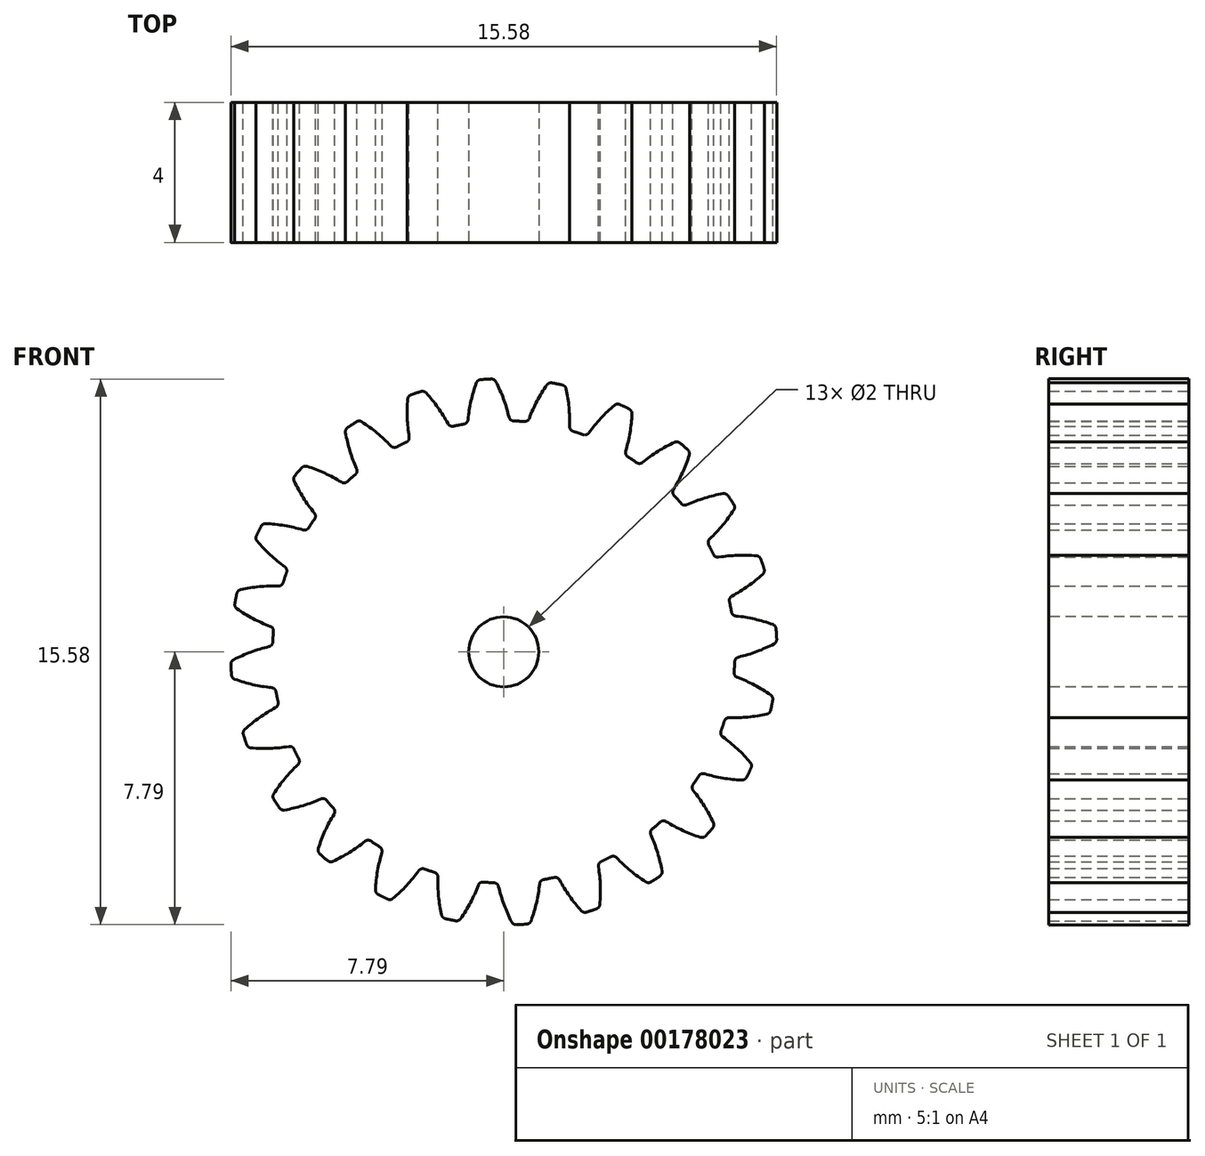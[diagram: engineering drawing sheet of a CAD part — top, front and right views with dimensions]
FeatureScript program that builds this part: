
annotation { "Feature Type Name" : "Feature", "Feature Type Description" : "" }
export const myFeature = defineFeature(function(context is Context, id is Id, definition is map)
    precondition{}
    {
        {
            var Q0;
            Q0=qCreatedBy(makeId("Front.planeOp"),FACE);
            var sketch = newSketch(context, id + "F0", { "sketchPlane" : qUnion([Q0])});
            skCircle(sketch, "E0", {"center": v(0, 0) * mm, "radius": 6.6 * mm, "construction": true});
            skCircle(sketch, "E1", {"center": v(0, 0) * mm, "radius": 7.2 * mm, "construction": true});
            skCircle(sketch, "E2", {"center": v(0, 0) * mm, "radius": 7.8 * mm, "construction": true});
            skLineSegment(sketch, "E3", {"start": v(0, 0) * mm, "end": v(0, 6.31) * mm, "construction": true});
            skCircle(sketch, "E4", {"center": v(0, 7.2) * mm, "radius": 4.32 * mm, "construction": true});
            skCircle(sketch, "E5.cCircle", {"center": v(0, 0) * mm, "radius": 6.31 * mm, "construction": true});
            skLineSegment(sketch, "E5.0", {"start": v(0, 6.31) * mm, "end": v(0.82, 6.26) * mm, "construction": true});
            skLineSegment(sketch, "E5.1", {"start": v(0.82, 6.26) * mm, "end": v(1.63, 6.1) * mm, "construction": true});
            skLineSegment(sketch, "E5.2", {"start": v(1.63, 6.1) * mm, "end": v(2.41, 5.83) * mm, "construction": true});
            skLineSegment(sketch, "E5.3", {"start": v(2.41, 5.83) * mm, "end": v(3.16, 5.46) * mm, "construction": true});
            skLineSegment(sketch, "E5.4", {"start": v(3.16, 5.46) * mm, "end": v(3.84, 5) * mm, "construction": true});
            skLineSegment(sketch, "E5.5", {"start": v(3.84, 5) * mm, "end": v(4.46, 4.46) * mm, "construction": true});
            skLineSegment(sketch, "E5.6", {"start": v(4.46, 4.46) * mm, "end": v(5, 3.84) * mm, "construction": true});
            skLineSegment(sketch, "E5.7", {"start": v(5, 3.84) * mm, "end": v(5.46, 3.16) * mm, "construction": true});
            skLineSegment(sketch, "E5.8", {"start": v(5.46, 3.16) * mm, "end": v(5.83, 2.41) * mm, "construction": true});
            skLineSegment(sketch, "E5.9", {"start": v(5.83, 2.41) * mm, "end": v(6.1, 1.63) * mm, "construction": true});
            skLineSegment(sketch, "E5.10", {"start": v(6.1, 1.63) * mm, "end": v(6.26, 0.82) * mm, "construction": true});
            skLineSegment(sketch, "E5.11", {"start": v(6.26, 0.82) * mm, "end": v(6.31, 0) * mm, "construction": true});
            skLineSegment(sketch, "E5.12", {"start": v(6.31, 0) * mm, "end": v(6.26, -0.82) * mm, "construction": true});
            skLineSegment(sketch, "E5.13", {"start": v(6.26, -0.82) * mm, "end": v(6.1, -1.63) * mm, "construction": true});
            skLineSegment(sketch, "E5.14", {"start": v(6.1, -1.63) * mm, "end": v(5.83, -2.41) * mm, "construction": true});
            skLineSegment(sketch, "E5.15", {"start": v(5.83, -2.41) * mm, "end": v(5.46, -3.16) * mm, "construction": true});
            skLineSegment(sketch, "E5.16", {"start": v(5.46, -3.16) * mm, "end": v(5, -3.84) * mm, "construction": true});
            skLineSegment(sketch, "E5.17", {"start": v(5, -3.84) * mm, "end": v(4.46, -4.46) * mm, "construction": true});
            skLineSegment(sketch, "E5.18", {"start": v(4.46, -4.46) * mm, "end": v(3.84, -5) * mm, "construction": true});
            skLineSegment(sketch, "E5.19", {"start": v(3.84, -5) * mm, "end": v(3.16, -5.46) * mm, "construction": true});
            skLineSegment(sketch, "E5.20", {"start": v(3.16, -5.46) * mm, "end": v(2.41, -5.83) * mm, "construction": true});
            skLineSegment(sketch, "E5.21", {"start": v(2.41, -5.83) * mm, "end": v(1.63, -6.1) * mm, "construction": true});
            skLineSegment(sketch, "E5.22", {"start": v(1.63, -6.1) * mm, "end": v(0.82, -6.26) * mm, "construction": true});
            skLineSegment(sketch, "E5.23", {"start": v(0.82, -6.26) * mm, "end": v(0, -6.31) * mm, "construction": true});
            skLineSegment(sketch, "E5.24", {"start": v(0, -6.31) * mm, "end": v(-0.82, -6.26) * mm, "construction": true});
            skLineSegment(sketch, "E5.25", {"start": v(-0.82, -6.26) * mm, "end": v(-1.63, -6.1) * mm, "construction": true});
            skLineSegment(sketch, "E5.26", {"start": v(-1.63, -6.1) * mm, "end": v(-2.41, -5.83) * mm, "construction": true});
            skLineSegment(sketch, "E5.27", {"start": v(-2.41, -5.83) * mm, "end": v(-3.16, -5.46) * mm, "construction": true});
            skLineSegment(sketch, "E5.28", {"start": v(-3.16, -5.46) * mm, "end": v(-3.84, -5) * mm, "construction": true});
            skLineSegment(sketch, "E5.29", {"start": v(-3.84, -5) * mm, "end": v(-4.46, -4.46) * mm, "construction": true});
            skLineSegment(sketch, "E5.30", {"start": v(-4.46, -4.46) * mm, "end": v(-5, -3.84) * mm, "construction": true});
            skLineSegment(sketch, "E5.31", {"start": v(-5, -3.84) * mm, "end": v(-5.46, -3.16) * mm, "construction": true});
            skLineSegment(sketch, "E5.32", {"start": v(-5.46, -3.16) * mm, "end": v(-5.83, -2.41) * mm, "construction": true});
            skLineSegment(sketch, "E5.33", {"start": v(-5.83, -2.41) * mm, "end": v(-6.1, -1.63) * mm, "construction": true});
            skLineSegment(sketch, "E5.34", {"start": v(-6.1, -1.63) * mm, "end": v(-6.26, -0.82) * mm, "construction": true});
            skLineSegment(sketch, "E5.35", {"start": v(-6.26, -0.82) * mm, "end": v(-6.31, 0) * mm, "construction": true});
            skLineSegment(sketch, "E5.36", {"start": v(-6.31, 0) * mm, "end": v(-6.26, 0.82) * mm, "construction": true});
            skLineSegment(sketch, "E5.37", {"start": v(-6.26, 0.82) * mm, "end": v(-6.1, 1.63) * mm, "construction": true});
            skLineSegment(sketch, "E5.38", {"start": v(-6.1, 1.63) * mm, "end": v(-5.83, 2.41) * mm, "construction": true});
            skLineSegment(sketch, "E5.39", {"start": v(-5.83, 2.41) * mm, "end": v(-5.46, 3.16) * mm, "construction": true});
            skLineSegment(sketch, "E5.40", {"start": v(-5.46, 3.16) * mm, "end": v(-5, 3.84) * mm, "construction": true});
            skLineSegment(sketch, "E5.41", {"start": v(-5, 3.84) * mm, "end": v(-4.46, 4.46) * mm, "construction": true});
            skLineSegment(sketch, "E5.42", {"start": v(-4.46, 4.46) * mm, "end": v(-3.84, 5) * mm, "construction": true});
            skLineSegment(sketch, "E5.43", {"start": v(-3.84, 5) * mm, "end": v(-3.16, 5.46) * mm, "construction": true});
            skLineSegment(sketch, "E5.44", {"start": v(-3.16, 5.46) * mm, "end": v(-2.41, 5.83) * mm, "construction": true});
            skLineSegment(sketch, "E5.45", {"start": v(-2.41, 5.83) * mm, "end": v(-1.63, 6.1) * mm, "construction": true});
            skLineSegment(sketch, "E5.46", {"start": v(-1.63, 6.1) * mm, "end": v(-0.82, 6.26) * mm, "construction": true});
            skLineSegment(sketch, "E5.47", {"start": v(-0.82, 6.26) * mm, "end": v(0, 6.31) * mm, "construction": true});
            skLineSegment(sketch, "E6.0", {"start": v(-0.41, 6.31) * mm, "end": v(0.41, 6.31) * mm});
            skLineSegment(sketch, "E6.1", {"start": v(0.41, 6.31) * mm, "end": v(1.23, 6.2) * mm});
            skLineSegment(sketch, "E6.2", {"start": v(1.23, 6.2) * mm, "end": v(2.03, 5.99) * mm});
            skLineSegment(sketch, "E6.3", {"start": v(2.03, 5.99) * mm, "end": v(2.8, 5.67) * mm});
            skLineSegment(sketch, "E6.4", {"start": v(2.8, 5.67) * mm, "end": v(3.51, 5.26) * mm});
            skLineSegment(sketch, "E6.5", {"start": v(3.51, 5.26) * mm, "end": v(4.17, 4.75) * mm});
            skLineSegment(sketch, "E6.6", {"start": v(4.17, 4.75) * mm, "end": v(4.75, 4.17) * mm});
            skLineSegment(sketch, "E6.7", {"start": v(4.75, 4.17) * mm, "end": v(5.26, 3.51) * mm, "construction": true});
            skLineSegment(sketch, "E6.8", {"start": v(5.26, 3.51) * mm, "end": v(5.67, 2.8) * mm});
            skLineSegment(sketch, "E6.9", {"start": v(5.67, 2.8) * mm, "end": v(5.99, 2.03) * mm});
            skLineSegment(sketch, "E6.10", {"start": v(5.99, 2.03) * mm, "end": v(6.2, 1.23) * mm});
            skLineSegment(sketch, "E6.11", {"start": v(6.2, 1.23) * mm, "end": v(6.31, 0.41) * mm});
            skLineSegment(sketch, "E6.12", {"start": v(6.31, 0.41) * mm, "end": v(6.31, -0.41) * mm});
            skLineSegment(sketch, "E6.13", {"start": v(6.31, -0.41) * mm, "end": v(6.2, -1.23) * mm});
            skLineSegment(sketch, "E6.14", {"start": v(6.2, -1.23) * mm, "end": v(5.99, -2.03) * mm});
            skLineSegment(sketch, "E6.15", {"start": v(5.99, -2.03) * mm, "end": v(5.67, -2.8) * mm});
            skLineSegment(sketch, "E6.16", {"start": v(5.67, -2.8) * mm, "end": v(5.26, -3.51) * mm});
            skLineSegment(sketch, "E6.17", {"start": v(5.26, -3.51) * mm, "end": v(4.75, -4.17) * mm});
            skLineSegment(sketch, "E6.18", {"start": v(4.75, -4.17) * mm, "end": v(4.17, -4.75) * mm});
            skLineSegment(sketch, "E6.19", {"start": v(4.17, -4.75) * mm, "end": v(3.51, -5.26) * mm});
            skLineSegment(sketch, "E6.20", {"start": v(3.51, -5.26) * mm, "end": v(2.8, -5.67) * mm});
            skLineSegment(sketch, "E6.21", {"start": v(2.8, -5.67) * mm, "end": v(2.03, -5.99) * mm});
            skLineSegment(sketch, "E6.22", {"start": v(2.03, -5.99) * mm, "end": v(1.23, -6.2) * mm});
            skLineSegment(sketch, "E6.23", {"start": v(1.23, -6.2) * mm, "end": v(0.41, -6.31) * mm});
            skLineSegment(sketch, "E6.24", {"start": v(0.41, -6.31) * mm, "end": v(-0.41, -6.31) * mm});
            skLineSegment(sketch, "E6.25", {"start": v(-0.41, -6.31) * mm, "end": v(-1.23, -6.2) * mm});
            skLineSegment(sketch, "E6.26", {"start": v(-1.23, -6.2) * mm, "end": v(-2.03, -5.99) * mm});
            skLineSegment(sketch, "E6.27", {"start": v(-2.03, -5.99) * mm, "end": v(-2.8, -5.67) * mm});
            skLineSegment(sketch, "E6.28", {"start": v(-2.8, -5.67) * mm, "end": v(-3.51, -5.26) * mm});
            skLineSegment(sketch, "E6.29", {"start": v(-3.51, -5.26) * mm, "end": v(-4.17, -4.75) * mm});
            skLineSegment(sketch, "E6.30", {"start": v(-4.17, -4.75) * mm, "end": v(-4.75, -4.17) * mm});
            skLineSegment(sketch, "E6.31", {"start": v(-4.75, -4.17) * mm, "end": v(-5.26, -3.51) * mm});
            skLineSegment(sketch, "E6.32", {"start": v(-5.26, -3.51) * mm, "end": v(-5.67, -2.8) * mm});
            skLineSegment(sketch, "E6.33", {"start": v(-5.67, -2.8) * mm, "end": v(-5.99, -2.03) * mm});
            skLineSegment(sketch, "E6.34", {"start": v(-5.99, -2.03) * mm, "end": v(-6.2, -1.23) * mm});
            skLineSegment(sketch, "E6.35", {"start": v(-6.2, -1.23) * mm, "end": v(-6.31, -0.41) * mm});
            skLineSegment(sketch, "E6.36", {"start": v(-6.31, -0.41) * mm, "end": v(-6.31, 0.41) * mm});
            skLineSegment(sketch, "E6.37", {"start": v(-6.31, 0.41) * mm, "end": v(-6.2, 1.23) * mm});
            skLineSegment(sketch, "E6.38", {"start": v(-6.2, 1.23) * mm, "end": v(-5.99, 2.03) * mm});
            skLineSegment(sketch, "E6.39", {"start": v(-5.99, 2.03) * mm, "end": v(-5.67, 2.8) * mm});
            skLineSegment(sketch, "E6.40", {"start": v(-5.67, 2.8) * mm, "end": v(-5.26, 3.51) * mm});
            skLineSegment(sketch, "E6.41", {"start": v(-5.26, 3.51) * mm, "end": v(-4.75, 4.17) * mm});
            skLineSegment(sketch, "E6.42", {"start": v(-4.75, 4.17) * mm, "end": v(-4.17, 4.75) * mm});
            skLineSegment(sketch, "E6.43", {"start": v(-4.17, 4.75) * mm, "end": v(-3.51, 5.26) * mm});
            skLineSegment(sketch, "E6.44", {"start": v(-3.51, 5.26) * mm, "end": v(-2.8, 5.67) * mm});
            skLineSegment(sketch, "E6.45", {"start": v(-2.8, 5.67) * mm, "end": v(-2.03, 5.99) * mm});
            skLineSegment(sketch, "E6.46", {"start": v(-2.03, 5.99) * mm, "end": v(-1.23, 6.2) * mm});
            skLineSegment(sketch, "E6.47", {"start": v(-1.23, 6.2) * mm, "end": v(-0.41, 6.31) * mm});
            skPoint(sketch, "E6.0.midPoint", {"position": v(0, 6.31) * mm});
            skLineSegment(sketch, "E7", {"start": v(0, 7.2) * mm, "end": v(-9.03, 7.2) * mm, "construction": true});
            skLineSegment(sketch, "E8", {"start": v(0, 7.2) * mm, "end": v(-8.97, 3.93) * mm, "construction": true});
            skCircle(sketch, "E9", {"center": v(-4.06, 5.72) * mm, "radius": 4.32 * mm, "construction": true});
            skArc(sketch, "E10", {"start": v(-0.23, 7.71) * mm, "mid": v(0, 7.22) * mm, "end": v(0.15, 6.7) * mm});
            skLineSegment(sketch, "E11", {"start": v(0, 0) * mm, "end": v(-0.41, 6.31) * mm, "construction": true});
            skArc(sketch, "E12.MirrorCS", {"start": v(-0.78, 7.68) * mm, "mid": v(-0.93, 7.16) * mm, "end": v(-1.02, 6.63) * mm});
            skArc(sketch, "E13", {"start": v(-0.66, 7.77) * mm, "mid": v(-0.51, 7.78) * mm, "end": v(-0.36, 7.8) * mm});
            skArc(sketch, "E14", {"start": v(-1.14, 6.5) * mm, "mid": v(0.43, -6.59) * mm, "end": v(0.28, 6.6) * mm});
            skPoint(sketch, "E15.visualSharp", {"position": v(-1.03, 6.52) * mm});
            skArc(sketch, "E15.filletArc", {"start": v(-1.14, 6.5) * mm, "mid": v(-1.06, 6.54) * mm, "end": v(-1.02, 6.63) * mm});
            skPoint(sketch, "E16.visualSharp", {"position": v(0.17, 6.6) * mm});
            skArc(sketch, "E16.filletArc", {"start": v(0.15, 6.7) * mm, "mid": v(0.2, 6.63) * mm, "end": v(0.28, 6.6) * mm});
            skPoint(sketch, "E17.visualSharp", {"position": v(-0.75, 7.76) * mm});
            skArc(sketch, "E17.filletArc", {"start": v(-0.66, 7.77) * mm, "mid": v(-0.74, 7.74) * mm, "end": v(-0.78, 7.68) * mm});
            skPoint(sketch, "E18.visualSharp", {"position": v(-0.27, 7.8) * mm});
            skArc(sketch, "E18.filletArc", {"start": v(-0.23, 7.71) * mm, "mid": v(-0.28, 7.77) * mm, "end": v(-0.36, 7.8) * mm});
            skArc(sketch, "E19.1.0", {"start": v(-2.78, 5.98) * mm, "mid": v(-2.72, 6.05) * mm, "end": v(-2.7, 6.14) * mm});
            skArc(sketch, "E19.1.1", {"start": v(-2.74, 7.21) * mm, "mid": v(-2.76, 6.67) * mm, "end": v(-2.7, 6.14) * mm});
            skArc(sketch, "E19.1.2", {"start": v(-2.65, 7.34) * mm, "mid": v(-2.71, 7.29) * mm, "end": v(-2.74, 7.21) * mm});
            skArc(sketch, "E19.1.3", {"start": v(-2.65, 7.34) * mm, "mid": v(-2.5, 7.39) * mm, "end": v(-2.36, 7.43) * mm});
            skArc(sketch, "E19.1.4", {"start": v(-2.21, 7.4) * mm, "mid": v(-2.28, 7.43) * mm, "end": v(-2.36, 7.43) * mm});
            skArc(sketch, "E19.1.5", {"start": v(-2.21, 7.4) * mm, "mid": v(-1.88, 6.97) * mm, "end": v(-1.6, 6.51) * mm});
            skArc(sketch, "E19.1.6", {"start": v(-1.6, 6.51) * mm, "mid": v(-1.53, 6.45) * mm, "end": v(-1.43, 6.44) * mm});
            skArc(sketch, "E19.2.0", {"start": v(-4.24, 5.06) * mm, "mid": v(-4.19, 5.14) * mm, "end": v(-4.2, 5.23) * mm});
            skArc(sketch, "E19.2.1", {"start": v(-4.52, 6.26) * mm, "mid": v(-4.39, 5.73) * mm, "end": v(-4.2, 5.23) * mm});
            skArc(sketch, "E19.2.2", {"start": v(-4.46, 6.4) * mm, "mid": v(-4.5, 6.34) * mm, "end": v(-4.52, 6.26) * mm});
            skArc(sketch, "E19.2.3", {"start": v(-4.46, 6.4) * mm, "mid": v(-4.33, 6.49) * mm, "end": v(-4.2, 6.57) * mm});
            skArc(sketch, "E19.2.4", {"start": v(-4.05, 6.57) * mm, "mid": v(-4.13, 6.6) * mm, "end": v(-4.2, 6.57) * mm});
            skArc(sketch, "E19.2.5", {"start": v(-4.05, 6.57) * mm, "mid": v(-3.62, 6.25) * mm, "end": v(-3.23, 5.88) * mm});
            skArc(sketch, "E19.2.6", {"start": v(-3.23, 5.88) * mm, "mid": v(-3.14, 5.84) * mm, "end": v(-3.05, 5.85) * mm});
            skArc(sketch, "E19.3.0", {"start": v(-5.4, 3.8) * mm, "mid": v(-5.38, 3.88) * mm, "end": v(-5.4, 3.96) * mm});
            skArc(sketch, "E19.3.1", {"start": v(-5.98, 4.88) * mm, "mid": v(-5.72, 4.4) * mm, "end": v(-5.4, 3.96) * mm});
            skArc(sketch, "E19.3.2", {"start": v(-5.96, 5.03) * mm, "mid": v(-6, 4.96) * mm, "end": v(-5.98, 4.88) * mm});
            skArc(sketch, "E19.3.3", {"start": v(-5.96, 5.03) * mm, "mid": v(-5.86, 5.14) * mm, "end": v(-5.76, 5.25) * mm});
            skArc(sketch, "E19.3.4", {"start": v(-5.61, 5.3) * mm, "mid": v(-5.7, 5.3) * mm, "end": v(-5.76, 5.25) * mm});
            skArc(sketch, "E19.3.5", {"start": v(-5.61, 5.3) * mm, "mid": v(-5.11, 5.1) * mm, "end": v(-4.64, 4.85) * mm});
            skArc(sketch, "E19.3.6", {"start": v(-4.64, 4.85) * mm, "mid": v(-4.55, 4.82) * mm, "end": v(-4.46, 4.86) * mm});
            skArc(sketch, "E19.4.0", {"start": v(-6.2, 2.26) * mm, "mid": v(-6.2, 2.36) * mm, "end": v(-6.25, 2.43) * mm});
            skArc(sketch, "E19.4.1", {"start": v(-7.04, 3.16) * mm, "mid": v(-6.67, 2.77) * mm, "end": v(-6.25, 2.43) * mm});
            skArc(sketch, "E19.4.2", {"start": v(-7.06, 3.31) * mm, "mid": v(-7.07, 3.23) * mm, "end": v(-7.04, 3.16) * mm});
            skArc(sketch, "E19.4.3", {"start": v(-7.06, 3.31) * mm, "mid": v(-7, 3.45) * mm, "end": v(-6.93, 3.58) * mm});
            skArc(sketch, "E19.4.4", {"start": v(-6.8, 3.66) * mm, "mid": v(-6.87, 3.64) * mm, "end": v(-6.93, 3.58) * mm});
            skArc(sketch, "E19.4.5", {"start": v(-6.8, 3.66) * mm, "mid": v(-6.26, 3.6) * mm, "end": v(-5.73, 3.48) * mm});
            skArc(sketch, "E19.4.6", {"start": v(-5.73, 3.48) * mm, "mid": v(-5.64, 3.48) * mm, "end": v(-5.57, 3.54) * mm});
            skArc(sketch, "E19.5.0", {"start": v(-6.57, 0.58) * mm, "mid": v(-6.6, 0.67) * mm, "end": v(-6.67, 0.73) * mm});
            skArc(sketch, "E19.5.1", {"start": v(-7.62, 1.23) * mm, "mid": v(-7.16, 0.95) * mm, "end": v(-6.67, 0.73) * mm});
            skArc(sketch, "E19.5.2", {"start": v(-7.68, 1.37) * mm, "mid": v(-7.67, 1.3) * mm, "end": v(-7.62, 1.23) * mm});
            skArc(sketch, "E19.5.3", {"start": v(-7.68, 1.37) * mm, "mid": v(-7.65, 1.52) * mm, "end": v(-7.62, 1.67) * mm});
            skArc(sketch, "E19.5.4", {"start": v(-7.5, 1.78) * mm, "mid": v(-7.58, 1.74) * mm, "end": v(-7.62, 1.67) * mm});
            skArc(sketch, "E19.5.5", {"start": v(-7.5, 1.78) * mm, "mid": v(-6.98, 1.86) * mm, "end": v(-6.44, 1.88) * mm});
            skArc(sketch, "E19.5.6", {"start": v(-6.44, 1.88) * mm, "mid": v(-6.35, 1.9) * mm, "end": v(-6.3, 1.98) * mm});
            skArc(sketch, "E19.6.0", {"start": v(-6.5, -1.14) * mm, "mid": v(-6.54, -1.06) * mm, "end": v(-6.63, -1.02) * mm});
            skArc(sketch, "E19.6.1", {"start": v(-7.68, -0.78) * mm, "mid": v(-7.16, -0.93) * mm, "end": v(-6.63, -1.02) * mm});
            skArc(sketch, "E19.6.2", {"start": v(-7.77, -0.66) * mm, "mid": v(-7.74, -0.74) * mm, "end": v(-7.68, -0.78) * mm});
            skArc(sketch, "E19.6.3", {"start": v(-7.77, -0.66) * mm, "mid": v(-7.78, -0.51) * mm, "end": v(-7.8, -0.36) * mm});
            skArc(sketch, "E19.6.4", {"start": v(-7.71, -0.23) * mm, "mid": v(-7.77, -0.28) * mm, "end": v(-7.8, -0.36) * mm});
            skArc(sketch, "E19.6.5", {"start": v(-7.71, -0.23) * mm, "mid": v(-7.22, 0) * mm, "end": v(-6.7, 0.15) * mm});
            skArc(sketch, "E19.6.6", {"start": v(-6.7, 0.15) * mm, "mid": v(-6.63, 0.2) * mm, "end": v(-6.6, 0.28) * mm});
            skArc(sketch, "E19.7.0", {"start": v(-5.98, -2.78) * mm, "mid": v(-6.05, -2.72) * mm, "end": v(-6.14, -2.7) * mm});
            skArc(sketch, "E19.7.1", {"start": v(-7.21, -2.74) * mm, "mid": v(-6.67, -2.76) * mm, "end": v(-6.14, -2.7) * mm});
            skArc(sketch, "E19.7.2", {"start": v(-7.34, -2.65) * mm, "mid": v(-7.29, -2.71) * mm, "end": v(-7.21, -2.74) * mm});
            skArc(sketch, "E19.7.3", {"start": v(-7.34, -2.65) * mm, "mid": v(-7.39, -2.5) * mm, "end": v(-7.43, -2.36) * mm});
            skArc(sketch, "E19.7.4", {"start": v(-7.4, -2.21) * mm, "mid": v(-7.43, -2.28) * mm, "end": v(-7.43, -2.36) * mm});
            skArc(sketch, "E19.7.5", {"start": v(-7.4, -2.21) * mm, "mid": v(-6.97, -1.88) * mm, "end": v(-6.51, -1.6) * mm});
            skArc(sketch, "E19.7.6", {"start": v(-6.51, -1.6) * mm, "mid": v(-6.45, -1.53) * mm, "end": v(-6.44, -1.43) * mm});
            skArc(sketch, "E19.8.0", {"start": v(-5.06, -4.24) * mm, "mid": v(-5.14, -4.19) * mm, "end": v(-5.23, -4.2) * mm});
            skArc(sketch, "E19.8.1", {"start": v(-6.26, -4.52) * mm, "mid": v(-5.73, -4.39) * mm, "end": v(-5.23, -4.2) * mm});
            skArc(sketch, "E19.8.2", {"start": v(-6.4, -4.46) * mm, "mid": v(-6.34, -4.5) * mm, "end": v(-6.26, -4.52) * mm});
            skArc(sketch, "E19.8.3", {"start": v(-6.4, -4.46) * mm, "mid": v(-6.49, -4.33) * mm, "end": v(-6.57, -4.2) * mm});
            skArc(sketch, "E19.8.4", {"start": v(-6.57, -4.05) * mm, "mid": v(-6.6, -4.13) * mm, "end": v(-6.57, -4.2) * mm});
            skArc(sketch, "E19.8.5", {"start": v(-6.57, -4.05) * mm, "mid": v(-6.25, -3.62) * mm, "end": v(-5.88, -3.23) * mm});
            skArc(sketch, "E19.8.6", {"start": v(-5.88, -3.23) * mm, "mid": v(-5.84, -3.14) * mm, "end": v(-5.85, -3.05) * mm});
            skArc(sketch, "E19.9.0", {"start": v(-3.8, -5.4) * mm, "mid": v(-3.88, -5.38) * mm, "end": v(-3.96, -5.4) * mm});
            skArc(sketch, "E19.9.1", {"start": v(-4.88, -5.98) * mm, "mid": v(-4.4, -5.72) * mm, "end": v(-3.96, -5.4) * mm});
            skArc(sketch, "E19.9.2", {"start": v(-5.03, -5.96) * mm, "mid": v(-4.96, -6) * mm, "end": v(-4.88, -5.98) * mm});
            skArc(sketch, "E19.9.3", {"start": v(-5.03, -5.96) * mm, "mid": v(-5.14, -5.86) * mm, "end": v(-5.25, -5.76) * mm});
            skArc(sketch, "E19.9.4", {"start": v(-5.3, -5.61) * mm, "mid": v(-5.3, -5.7) * mm, "end": v(-5.25, -5.76) * mm});
            skArc(sketch, "E19.9.5", {"start": v(-5.3, -5.61) * mm, "mid": v(-5.1, -5.11) * mm, "end": v(-4.85, -4.64) * mm});
            skArc(sketch, "E19.9.6", {"start": v(-4.85, -4.64) * mm, "mid": v(-4.82, -4.55) * mm, "end": v(-4.86, -4.46) * mm});
            skArc(sketch, "E19.10.0", {"start": v(-2.26, -6.2) * mm, "mid": v(-2.36, -6.2) * mm, "end": v(-2.43, -6.25) * mm});
            skArc(sketch, "E19.10.1", {"start": v(-3.16, -7.04) * mm, "mid": v(-2.77, -6.67) * mm, "end": v(-2.43, -6.25) * mm});
            skArc(sketch, "E19.10.2", {"start": v(-3.31, -7.06) * mm, "mid": v(-3.23, -7.07) * mm, "end": v(-3.16, -7.04) * mm});
            skArc(sketch, "E19.10.3", {"start": v(-3.31, -7.06) * mm, "mid": v(-3.45, -7) * mm, "end": v(-3.58, -6.93) * mm});
            skArc(sketch, "E19.10.4", {"start": v(-3.66, -6.8) * mm, "mid": v(-3.64, -6.87) * mm, "end": v(-3.58, -6.93) * mm});
            skArc(sketch, "E19.10.5", {"start": v(-3.66, -6.8) * mm, "mid": v(-3.6, -6.26) * mm, "end": v(-3.48, -5.73) * mm});
            skArc(sketch, "E19.10.6", {"start": v(-3.48, -5.73) * mm, "mid": v(-3.48, -5.64) * mm, "end": v(-3.54, -5.57) * mm});
            skArc(sketch, "E19.11.0", {"start": v(-0.58, -6.57) * mm, "mid": v(-0.67, -6.6) * mm, "end": v(-0.73, -6.67) * mm});
            skArc(sketch, "E19.11.1", {"start": v(-1.23, -7.62) * mm, "mid": v(-0.95, -7.16) * mm, "end": v(-0.73, -6.67) * mm});
            skArc(sketch, "E19.11.2", {"start": v(-1.37, -7.68) * mm, "mid": v(-1.3, -7.67) * mm, "end": v(-1.23, -7.62) * mm});
            skArc(sketch, "E19.11.3", {"start": v(-1.37, -7.68) * mm, "mid": v(-1.52, -7.65) * mm, "end": v(-1.67, -7.62) * mm});
            skArc(sketch, "E19.11.4", {"start": v(-1.78, -7.5) * mm, "mid": v(-1.74, -7.58) * mm, "end": v(-1.67, -7.62) * mm});
            skArc(sketch, "E19.11.5", {"start": v(-1.78, -7.5) * mm, "mid": v(-1.86, -6.98) * mm, "end": v(-1.88, -6.44) * mm});
            skArc(sketch, "E19.11.6", {"start": v(-1.88, -6.44) * mm, "mid": v(-1.9, -6.35) * mm, "end": v(-1.98, -6.3) * mm});
            skArc(sketch, "E19.12.0", {"start": v(1.14, -6.5) * mm, "mid": v(1.06, -6.54) * mm, "end": v(1.02, -6.63) * mm});
            skArc(sketch, "E19.12.1", {"start": v(0.78, -7.68) * mm, "mid": v(0.93, -7.16) * mm, "end": v(1.02, -6.63) * mm});
            skArc(sketch, "E19.12.2", {"start": v(0.66, -7.77) * mm, "mid": v(0.74, -7.74) * mm, "end": v(0.78, -7.68) * mm});
            skArc(sketch, "E19.12.3", {"start": v(0.66, -7.77) * mm, "mid": v(0.51, -7.78) * mm, "end": v(0.36, -7.8) * mm});
            skArc(sketch, "E19.12.4", {"start": v(0.23, -7.71) * mm, "mid": v(0.28, -7.77) * mm, "end": v(0.36, -7.8) * mm});
            skArc(sketch, "E19.12.5", {"start": v(0.23, -7.71) * mm, "mid": v(0, -7.22) * mm, "end": v(-0.15, -6.7) * mm});
            skArc(sketch, "E19.12.6", {"start": v(-0.15, -6.7) * mm, "mid": v(-0.2, -6.63) * mm, "end": v(-0.28, -6.6) * mm});
            skArc(sketch, "E19.13.0", {"start": v(2.78, -5.98) * mm, "mid": v(2.72, -6.05) * mm, "end": v(2.7, -6.14) * mm});
            skArc(sketch, "E19.13.1", {"start": v(2.74, -7.21) * mm, "mid": v(2.76, -6.67) * mm, "end": v(2.7, -6.14) * mm});
            skArc(sketch, "E19.13.2", {"start": v(2.65, -7.34) * mm, "mid": v(2.71, -7.29) * mm, "end": v(2.74, -7.21) * mm});
            skArc(sketch, "E19.13.3", {"start": v(2.65, -7.34) * mm, "mid": v(2.5, -7.39) * mm, "end": v(2.36, -7.43) * mm});
            skArc(sketch, "E19.13.4", {"start": v(2.21, -7.4) * mm, "mid": v(2.28, -7.43) * mm, "end": v(2.36, -7.43) * mm});
            skArc(sketch, "E19.13.5", {"start": v(2.21, -7.4) * mm, "mid": v(1.88, -6.97) * mm, "end": v(1.6, -6.51) * mm});
            skArc(sketch, "E19.13.6", {"start": v(1.6, -6.51) * mm, "mid": v(1.53, -6.45) * mm, "end": v(1.43, -6.44) * mm});
            skArc(sketch, "E19.14.0", {"start": v(4.24, -5.06) * mm, "mid": v(4.19, -5.14) * mm, "end": v(4.2, -5.23) * mm});
            skArc(sketch, "E19.14.1", {"start": v(4.52, -6.26) * mm, "mid": v(4.39, -5.73) * mm, "end": v(4.2, -5.23) * mm});
            skArc(sketch, "E19.14.2", {"start": v(4.46, -6.4) * mm, "mid": v(4.5, -6.34) * mm, "end": v(4.52, -6.26) * mm});
            skArc(sketch, "E19.14.3", {"start": v(4.46, -6.4) * mm, "mid": v(4.33, -6.49) * mm, "end": v(4.2, -6.57) * mm});
            skArc(sketch, "E19.14.4", {"start": v(4.05, -6.57) * mm, "mid": v(4.13, -6.6) * mm, "end": v(4.2, -6.57) * mm});
            skArc(sketch, "E19.14.5", {"start": v(4.05, -6.57) * mm, "mid": v(3.62, -6.25) * mm, "end": v(3.23, -5.88) * mm});
            skArc(sketch, "E19.14.6", {"start": v(3.23, -5.88) * mm, "mid": v(3.14, -5.84) * mm, "end": v(3.05, -5.85) * mm});
            skArc(sketch, "E19.15.0", {"start": v(5.4, -3.8) * mm, "mid": v(5.38, -3.88) * mm, "end": v(5.4, -3.96) * mm});
            skArc(sketch, "E19.15.1", {"start": v(5.98, -4.88) * mm, "mid": v(5.72, -4.4) * mm, "end": v(5.4, -3.96) * mm});
            skArc(sketch, "E19.15.2", {"start": v(5.96, -5.03) * mm, "mid": v(6, -4.96) * mm, "end": v(5.98, -4.88) * mm});
            skArc(sketch, "E19.15.3", {"start": v(5.96, -5.03) * mm, "mid": v(5.86, -5.14) * mm, "end": v(5.76, -5.25) * mm});
            skArc(sketch, "E19.15.4", {"start": v(5.61, -5.3) * mm, "mid": v(5.7, -5.3) * mm, "end": v(5.76, -5.25) * mm});
            skArc(sketch, "E19.15.5", {"start": v(5.61, -5.3) * mm, "mid": v(5.11, -5.1) * mm, "end": v(4.64, -4.85) * mm});
            skArc(sketch, "E19.15.6", {"start": v(4.64, -4.85) * mm, "mid": v(4.55, -4.82) * mm, "end": v(4.46, -4.86) * mm});
            skArc(sketch, "E19.16.0", {"start": v(6.2, -2.26) * mm, "mid": v(6.2, -2.36) * mm, "end": v(6.25, -2.43) * mm});
            skArc(sketch, "E19.16.1", {"start": v(7.04, -3.16) * mm, "mid": v(6.67, -2.77) * mm, "end": v(6.25, -2.43) * mm});
            skArc(sketch, "E19.16.2", {"start": v(7.06, -3.31) * mm, "mid": v(7.07, -3.23) * mm, "end": v(7.04, -3.16) * mm});
            skArc(sketch, "E19.16.3", {"start": v(7.06, -3.31) * mm, "mid": v(7, -3.45) * mm, "end": v(6.93, -3.58) * mm});
            skArc(sketch, "E19.16.4", {"start": v(6.8, -3.66) * mm, "mid": v(6.87, -3.64) * mm, "end": v(6.93, -3.58) * mm});
            skArc(sketch, "E19.16.5", {"start": v(6.8, -3.66) * mm, "mid": v(6.26, -3.6) * mm, "end": v(5.73, -3.48) * mm});
            skArc(sketch, "E19.16.6", {"start": v(5.73, -3.48) * mm, "mid": v(5.64, -3.48) * mm, "end": v(5.57, -3.54) * mm});
            skArc(sketch, "E19.17.0", {"start": v(6.57, -0.58) * mm, "mid": v(6.6, -0.67) * mm, "end": v(6.67, -0.73) * mm});
            skArc(sketch, "E19.17.1", {"start": v(7.62, -1.23) * mm, "mid": v(7.16, -0.95) * mm, "end": v(6.67, -0.73) * mm});
            skArc(sketch, "E19.17.2", {"start": v(7.68, -1.37) * mm, "mid": v(7.67, -1.3) * mm, "end": v(7.62, -1.23) * mm});
            skArc(sketch, "E19.17.3", {"start": v(7.68, -1.37) * mm, "mid": v(7.65, -1.52) * mm, "end": v(7.62, -1.67) * mm});
            skArc(sketch, "E19.17.4", {"start": v(7.5, -1.78) * mm, "mid": v(7.58, -1.74) * mm, "end": v(7.62, -1.67) * mm});
            skArc(sketch, "E19.17.5", {"start": v(7.5, -1.78) * mm, "mid": v(6.98, -1.86) * mm, "end": v(6.44, -1.88) * mm});
            skArc(sketch, "E19.17.6", {"start": v(6.44, -1.88) * mm, "mid": v(6.35, -1.9) * mm, "end": v(6.3, -1.98) * mm});
            skArc(sketch, "E19.18.0", {"start": v(6.5, 1.14) * mm, "mid": v(6.54, 1.06) * mm, "end": v(6.63, 1.02) * mm});
            skArc(sketch, "E19.18.1", {"start": v(7.68, 0.78) * mm, "mid": v(7.16, 0.93) * mm, "end": v(6.63, 1.02) * mm});
            skArc(sketch, "E19.18.2", {"start": v(7.77, 0.66) * mm, "mid": v(7.74, 0.74) * mm, "end": v(7.68, 0.78) * mm});
            skArc(sketch, "E19.18.3", {"start": v(7.77, 0.66) * mm, "mid": v(7.78, 0.51) * mm, "end": v(7.8, 0.36) * mm});
            skArc(sketch, "E19.18.4", {"start": v(7.71, 0.23) * mm, "mid": v(7.77, 0.28) * mm, "end": v(7.8, 0.36) * mm});
            skArc(sketch, "E19.18.5", {"start": v(7.71, 0.23) * mm, "mid": v(7.22, 0) * mm, "end": v(6.7, -0.15) * mm});
            skArc(sketch, "E19.18.6", {"start": v(6.7, -0.15) * mm, "mid": v(6.63, -0.2) * mm, "end": v(6.6, -0.28) * mm});
            skArc(sketch, "E19.19.0", {"start": v(5.98, 2.78) * mm, "mid": v(6.05, 2.72) * mm, "end": v(6.14, 2.7) * mm});
            skArc(sketch, "E19.19.1", {"start": v(7.21, 2.74) * mm, "mid": v(6.67, 2.76) * mm, "end": v(6.14, 2.7) * mm});
            skArc(sketch, "E19.19.2", {"start": v(7.34, 2.65) * mm, "mid": v(7.29, 2.71) * mm, "end": v(7.21, 2.74) * mm});
            skArc(sketch, "E19.19.3", {"start": v(7.34, 2.65) * mm, "mid": v(7.39, 2.5) * mm, "end": v(7.43, 2.36) * mm});
            skArc(sketch, "E19.19.4", {"start": v(7.4, 2.21) * mm, "mid": v(7.43, 2.28) * mm, "end": v(7.43, 2.36) * mm});
            skArc(sketch, "E19.19.5", {"start": v(7.4, 2.21) * mm, "mid": v(6.97, 1.88) * mm, "end": v(6.51, 1.6) * mm});
            skArc(sketch, "E19.19.6", {"start": v(6.51, 1.6) * mm, "mid": v(6.45, 1.53) * mm, "end": v(6.44, 1.43) * mm});
            skArc(sketch, "E19.20.0", {"start": v(5.06, 4.24) * mm, "mid": v(5.14, 4.19) * mm, "end": v(5.23, 4.2) * mm});
            skArc(sketch, "E19.20.1", {"start": v(6.26, 4.52) * mm, "mid": v(5.73, 4.39) * mm, "end": v(5.23, 4.2) * mm});
            skArc(sketch, "E19.20.2", {"start": v(6.4, 4.46) * mm, "mid": v(6.34, 4.5) * mm, "end": v(6.26, 4.52) * mm});
            skArc(sketch, "E19.20.3", {"start": v(6.4, 4.46) * mm, "mid": v(6.49, 4.33) * mm, "end": v(6.57, 4.2) * mm});
            skArc(sketch, "E19.20.4", {"start": v(6.57, 4.05) * mm, "mid": v(6.6, 4.13) * mm, "end": v(6.57, 4.2) * mm});
            skArc(sketch, "E19.20.5", {"start": v(6.57, 4.05) * mm, "mid": v(6.25, 3.62) * mm, "end": v(5.88, 3.23) * mm});
            skArc(sketch, "E19.20.6", {"start": v(5.88, 3.23) * mm, "mid": v(5.84, 3.14) * mm, "end": v(5.85, 3.05) * mm});
            skArc(sketch, "E19.21.0", {"start": v(3.8, 5.4) * mm, "mid": v(3.88, 5.38) * mm, "end": v(3.96, 5.4) * mm});
            skArc(sketch, "E19.21.1", {"start": v(4.88, 5.98) * mm, "mid": v(4.4, 5.72) * mm, "end": v(3.96, 5.4) * mm});
            skArc(sketch, "E19.21.2", {"start": v(5.03, 5.96) * mm, "mid": v(4.96, 6) * mm, "end": v(4.88, 5.98) * mm});
            skArc(sketch, "E19.21.3", {"start": v(5.03, 5.96) * mm, "mid": v(5.14, 5.86) * mm, "end": v(5.25, 5.76) * mm});
            skArc(sketch, "E19.21.4", {"start": v(5.3, 5.61) * mm, "mid": v(5.3, 5.7) * mm, "end": v(5.25, 5.76) * mm});
            skArc(sketch, "E19.21.5", {"start": v(5.3, 5.61) * mm, "mid": v(5.1, 5.11) * mm, "end": v(4.85, 4.64) * mm});
            skArc(sketch, "E19.21.6", {"start": v(4.85, 4.64) * mm, "mid": v(4.82, 4.55) * mm, "end": v(4.86, 4.46) * mm});
            skArc(sketch, "E19.22.0", {"start": v(2.26, 6.2) * mm, "mid": v(2.36, 6.2) * mm, "end": v(2.43, 6.25) * mm});
            skArc(sketch, "E19.22.1", {"start": v(3.16, 7.04) * mm, "mid": v(2.77, 6.67) * mm, "end": v(2.43, 6.25) * mm});
            skArc(sketch, "E19.22.2", {"start": v(3.31, 7.06) * mm, "mid": v(3.23, 7.07) * mm, "end": v(3.16, 7.04) * mm});
            skArc(sketch, "E19.22.3", {"start": v(3.31, 7.06) * mm, "mid": v(3.45, 7) * mm, "end": v(3.58, 6.93) * mm});
            skArc(sketch, "E19.22.4", {"start": v(3.66, 6.8) * mm, "mid": v(3.64, 6.87) * mm, "end": v(3.58, 6.93) * mm});
            skArc(sketch, "E19.22.5", {"start": v(3.66, 6.8) * mm, "mid": v(3.6, 6.26) * mm, "end": v(3.48, 5.73) * mm});
            skArc(sketch, "E19.22.6", {"start": v(3.48, 5.73) * mm, "mid": v(3.48, 5.64) * mm, "end": v(3.54, 5.57) * mm});
            skArc(sketch, "E19.23.0", {"start": v(0.58, 6.57) * mm, "mid": v(0.67, 6.6) * mm, "end": v(0.73, 6.67) * mm});
            skArc(sketch, "E19.23.1", {"start": v(1.23, 7.62) * mm, "mid": v(0.95, 7.16) * mm, "end": v(0.73, 6.67) * mm});
            skArc(sketch, "E19.23.2", {"start": v(1.37, 7.68) * mm, "mid": v(1.3, 7.67) * mm, "end": v(1.23, 7.62) * mm});
            skArc(sketch, "E19.23.3", {"start": v(1.37, 7.68) * mm, "mid": v(1.52, 7.65) * mm, "end": v(1.67, 7.62) * mm});
            skArc(sketch, "E19.23.4", {"start": v(1.78, 7.5) * mm, "mid": v(1.74, 7.58) * mm, "end": v(1.67, 7.62) * mm});
            skArc(sketch, "E19.23.5", {"start": v(1.78, 7.5) * mm, "mid": v(1.86, 6.98) * mm, "end": v(1.88, 6.44) * mm});
            skArc(sketch, "E19.23.6", {"start": v(1.88, 6.44) * mm, "mid": v(1.9, 6.35) * mm, "end": v(1.98, 6.3) * mm});
            skSolve(sketch);
        }
        {
            var Q0;
            Q0=qSketchRegion(id+"F0",true);
            extrude(context, id + "F1", {"entities" : qUnion([Q0]), "depth" : 4 * mm});
        }
        {
            var Q0;
            Q0=makeQuery(id+"F1.opExtrude","CAP_FACE",FACE,{"disambiguationData":[OSD([sQuery(id+"F0.wireOp",EDGE,"E10"),sQuery(id+"F0.wireOp",EDGE,"E12.MirrorCS"),sQuery(id+"F0.wireOp",EDGE,"E13"),sQuery(id+"F0.wireOp",EDGE,"E14"),sQuery(id+"F0.wireOp",EDGE,"E15.filletArc"),sQuery(id+"F0.wireOp",EDGE,"E16.filletArc"),sQuery(id+"F0.wireOp",EDGE,"E17.filletArc"),sQuery(id+"F0.wireOp",EDGE,"E18.filletArc"),sQuery(id+"F0.wireOp",EDGE,"E19.1.0"),sQuery(id+"F0.wireOp",EDGE,"E19.1.1"),sQuery(id+"F0.wireOp",EDGE,"E19.1.2"),sQuery(id+"F0.wireOp",EDGE,"E19.1.3"),sQuery(id+"F0.wireOp",EDGE,"E19.1.4"),sQuery(id+"F0.wireOp",EDGE,"E19.1.5"),sQuery(id+"F0.wireOp",EDGE,"E19.1.6"),sQuery(id+"F0.wireOp",EDGE,"E19.2.0"),sQuery(id+"F0.wireOp",EDGE,"E19.2.1"),sQuery(id+"F0.wireOp",EDGE,"E19.2.2"),sQuery(id+"F0.wireOp",EDGE,"E19.2.3"),sQuery(id+"F0.wireOp",EDGE,"E19.2.4"),sQuery(id+"F0.wireOp",EDGE,"E19.2.5"),sQuery(id+"F0.wireOp",EDGE,"E19.2.6"),sQuery(id+"F0.wireOp",EDGE,"E19.3.0"),sQuery(id+"F0.wireOp",EDGE,"E19.3.1"),sQuery(id+"F0.wireOp",EDGE,"E19.3.2"),sQuery(id+"F0.wireOp",EDGE,"E19.3.3"),sQuery(id+"F0.wireOp",EDGE,"E19.3.4"),sQuery(id+"F0.wireOp",EDGE,"E19.3.5"),sQuery(id+"F0.wireOp",EDGE,"E19.3.6"),sQuery(id+"F0.wireOp",EDGE,"E19.4.0"),sQuery(id+"F0.wireOp",EDGE,"E19.4.1"),sQuery(id+"F0.wireOp",EDGE,"E19.4.2"),sQuery(id+"F0.wireOp",EDGE,"E19.4.3"),sQuery(id+"F0.wireOp",EDGE,"E19.4.4"),sQuery(id+"F0.wireOp",EDGE,"E19.4.5"),sQuery(id+"F0.wireOp",EDGE,"E19.4.6"),sQuery(id+"F0.wireOp",EDGE,"E19.5.0"),sQuery(id+"F0.wireOp",EDGE,"E19.5.1"),sQuery(id+"F0.wireOp",EDGE,"E19.5.2"),sQuery(id+"F0.wireOp",EDGE,"E19.5.3"),sQuery(id+"F0.wireOp",EDGE,"E19.5.4"),sQuery(id+"F0.wireOp",EDGE,"E19.5.5"),sQuery(id+"F0.wireOp",EDGE,"E19.5.6"),sQuery(id+"F0.wireOp",EDGE,"E19.6.0"),sQuery(id+"F0.wireOp",EDGE,"E19.6.1"),sQuery(id+"F0.wireOp",EDGE,"E19.6.2"),sQuery(id+"F0.wireOp",EDGE,"E19.6.3"),sQuery(id+"F0.wireOp",EDGE,"E19.6.4"),sQuery(id+"F0.wireOp",EDGE,"E19.6.5"),sQuery(id+"F0.wireOp",EDGE,"E19.6.6"),sQuery(id+"F0.wireOp",EDGE,"E19.7.0"),sQuery(id+"F0.wireOp",EDGE,"E19.7.1"),sQuery(id+"F0.wireOp",EDGE,"E19.7.2"),sQuery(id+"F0.wireOp",EDGE,"E19.7.3"),sQuery(id+"F0.wireOp",EDGE,"E19.7.4"),sQuery(id+"F0.wireOp",EDGE,"E19.7.5"),sQuery(id+"F0.wireOp",EDGE,"E19.7.6"),sQuery(id+"F0.wireOp",EDGE,"E19.8.0"),sQuery(id+"F0.wireOp",EDGE,"E19.8.1"),sQuery(id+"F0.wireOp",EDGE,"E19.8.2"),sQuery(id+"F0.wireOp",EDGE,"E19.8.3"),sQuery(id+"F0.wireOp",EDGE,"E19.8.4"),sQuery(id+"F0.wireOp",EDGE,"E19.8.5"),sQuery(id+"F0.wireOp",EDGE,"E19.8.6"),sQuery(id+"F0.wireOp",EDGE,"E19.9.0"),sQuery(id+"F0.wireOp",EDGE,"E19.9.1"),sQuery(id+"F0.wireOp",EDGE,"E19.9.2"),sQuery(id+"F0.wireOp",EDGE,"E19.9.3"),sQuery(id+"F0.wireOp",EDGE,"E19.9.4"),sQuery(id+"F0.wireOp",EDGE,"E19.9.5"),sQuery(id+"F0.wireOp",EDGE,"E19.9.6"),sQuery(id+"F0.wireOp",EDGE,"E19.10.0"),sQuery(id+"F0.wireOp",EDGE,"E19.10.1"),sQuery(id+"F0.wireOp",EDGE,"E19.10.2"),sQuery(id+"F0.wireOp",EDGE,"E19.10.3"),sQuery(id+"F0.wireOp",EDGE,"E19.10.4"),sQuery(id+"F0.wireOp",EDGE,"E19.10.5"),sQuery(id+"F0.wireOp",EDGE,"E19.10.6"),sQuery(id+"F0.wireOp",EDGE,"E19.11.0"),sQuery(id+"F0.wireOp",EDGE,"E19.11.1"),sQuery(id+"F0.wireOp",EDGE,"E19.11.2"),sQuery(id+"F0.wireOp",EDGE,"E19.11.3"),sQuery(id+"F0.wireOp",EDGE,"E19.11.4"),sQuery(id+"F0.wireOp",EDGE,"E19.11.5"),sQuery(id+"F0.wireOp",EDGE,"E19.11.6"),sQuery(id+"F0.wireOp",EDGE,"E19.12.0"),sQuery(id+"F0.wireOp",EDGE,"E19.12.1"),sQuery(id+"F0.wireOp",EDGE,"E19.12.2"),sQuery(id+"F0.wireOp",EDGE,"E19.12.3"),sQuery(id+"F0.wireOp",EDGE,"E19.12.4"),sQuery(id+"F0.wireOp",EDGE,"E19.12.5"),sQuery(id+"F0.wireOp",EDGE,"E19.12.6"),sQuery(id+"F0.wireOp",EDGE,"E19.13.0"),sQuery(id+"F0.wireOp",EDGE,"E19.13.1"),sQuery(id+"F0.wireOp",EDGE,"E19.13.2"),sQuery(id+"F0.wireOp",EDGE,"E19.13.3"),sQuery(id+"F0.wireOp",EDGE,"E19.13.4"),sQuery(id+"F0.wireOp",EDGE,"E19.13.5"),sQuery(id+"F0.wireOp",EDGE,"E19.13.6"),sQuery(id+"F0.wireOp",EDGE,"E19.14.0"),sQuery(id+"F0.wireOp",EDGE,"E19.14.1"),sQuery(id+"F0.wireOp",EDGE,"E19.14.2"),sQuery(id+"F0.wireOp",EDGE,"E19.14.3"),sQuery(id+"F0.wireOp",EDGE,"E19.14.4"),sQuery(id+"F0.wireOp",EDGE,"E19.14.5"),sQuery(id+"F0.wireOp",EDGE,"E19.14.6"),sQuery(id+"F0.wireOp",EDGE,"E19.15.0"),sQuery(id+"F0.wireOp",EDGE,"E19.15.1"),sQuery(id+"F0.wireOp",EDGE,"E19.15.2"),sQuery(id+"F0.wireOp",EDGE,"E19.15.3"),sQuery(id+"F0.wireOp",EDGE,"E19.15.4"),sQuery(id+"F0.wireOp",EDGE,"E19.15.5"),sQuery(id+"F0.wireOp",EDGE,"E19.15.6"),sQuery(id+"F0.wireOp",EDGE,"E19.16.0"),sQuery(id+"F0.wireOp",EDGE,"E19.16.1"),sQuery(id+"F0.wireOp",EDGE,"E19.16.2"),sQuery(id+"F0.wireOp",EDGE,"E19.16.3"),sQuery(id+"F0.wireOp",EDGE,"E19.16.4"),sQuery(id+"F0.wireOp",EDGE,"E19.16.5"),sQuery(id+"F0.wireOp",EDGE,"E19.16.6"),sQuery(id+"F0.wireOp",EDGE,"E19.17.0"),sQuery(id+"F0.wireOp",EDGE,"E19.17.1"),sQuery(id+"F0.wireOp",EDGE,"E19.17.2"),sQuery(id+"F0.wireOp",EDGE,"E19.17.3"),sQuery(id+"F0.wireOp",EDGE,"E19.17.4"),sQuery(id+"F0.wireOp",EDGE,"E19.17.5"),sQuery(id+"F0.wireOp",EDGE,"E19.17.6"),sQuery(id+"F0.wireOp",EDGE,"E19.18.0"),sQuery(id+"F0.wireOp",EDGE,"E19.18.1"),sQuery(id+"F0.wireOp",EDGE,"E19.18.2"),sQuery(id+"F0.wireOp",EDGE,"E19.18.3"),sQuery(id+"F0.wireOp",EDGE,"E19.18.4"),sQuery(id+"F0.wireOp",EDGE,"E19.18.5"),sQuery(id+"F0.wireOp",EDGE,"E19.18.6"),sQuery(id+"F0.wireOp",EDGE,"E19.19.0"),sQuery(id+"F0.wireOp",EDGE,"E19.19.1"),sQuery(id+"F0.wireOp",EDGE,"E19.19.2"),sQuery(id+"F0.wireOp",EDGE,"E19.19.3"),sQuery(id+"F0.wireOp",EDGE,"E19.19.4"),sQuery(id+"F0.wireOp",EDGE,"E19.19.5"),sQuery(id+"F0.wireOp",EDGE,"E19.19.6"),sQuery(id+"F0.wireOp",EDGE,"E19.20.0"),sQuery(id+"F0.wireOp",EDGE,"E19.20.1"),sQuery(id+"F0.wireOp",EDGE,"E19.20.2"),sQuery(id+"F0.wireOp",EDGE,"E19.20.3"),sQuery(id+"F0.wireOp",EDGE,"E19.20.4"),sQuery(id+"F0.wireOp",EDGE,"E19.20.5"),sQuery(id+"F0.wireOp",EDGE,"E19.20.6"),sQuery(id+"F0.wireOp",EDGE,"E19.21.0"),sQuery(id+"F0.wireOp",EDGE,"E19.21.1"),sQuery(id+"F0.wireOp",EDGE,"E19.21.2"),sQuery(id+"F0.wireOp",EDGE,"E19.21.3"),sQuery(id+"F0.wireOp",EDGE,"E19.21.4"),sQuery(id+"F0.wireOp",EDGE,"E19.21.5"),sQuery(id+"F0.wireOp",EDGE,"E19.21.6"),sQuery(id+"F0.wireOp",EDGE,"E19.22.0"),sQuery(id+"F0.wireOp",EDGE,"E19.22.1"),sQuery(id+"F0.wireOp",EDGE,"E19.22.2"),sQuery(id+"F0.wireOp",EDGE,"E19.22.3"),sQuery(id+"F0.wireOp",EDGE,"E19.22.4"),sQuery(id+"F0.wireOp",EDGE,"E19.22.5"),sQuery(id+"F0.wireOp",EDGE,"E19.22.6"),sQuery(id+"F0.wireOp",EDGE,"E19.23.0"),sQuery(id+"F0.wireOp",EDGE,"E19.23.1"),sQuery(id+"F0.wireOp",EDGE,"E19.23.2"),sQuery(id+"F0.wireOp",EDGE,"E19.23.3"),sQuery(id+"F0.wireOp",EDGE,"E19.23.4"),sQuery(id+"F0.wireOp",EDGE,"E19.23.5"),sQuery(id+"F0.wireOp",EDGE,"E19.23.6")])],"isStart":false});
            var sketch = newSketch(context, id + "F2", { "sketchPlane" : qUnion([Q0])});
            skCircle(sketch, "E20", {"center": v(0, 0) * mm, "radius": 1 * mm});
            skSolve(sketch);
        }
        {
            var Q0;
            Q0=qSketchRegion(id+"F2",true);
            extrude(context, id + "F3", {"entities" : qUnion([Q0]), "operationType" : NewBodyOperationType.REMOVE, "oppositeDirection" : true, "depth" : 25 * mm});
        }
    });
